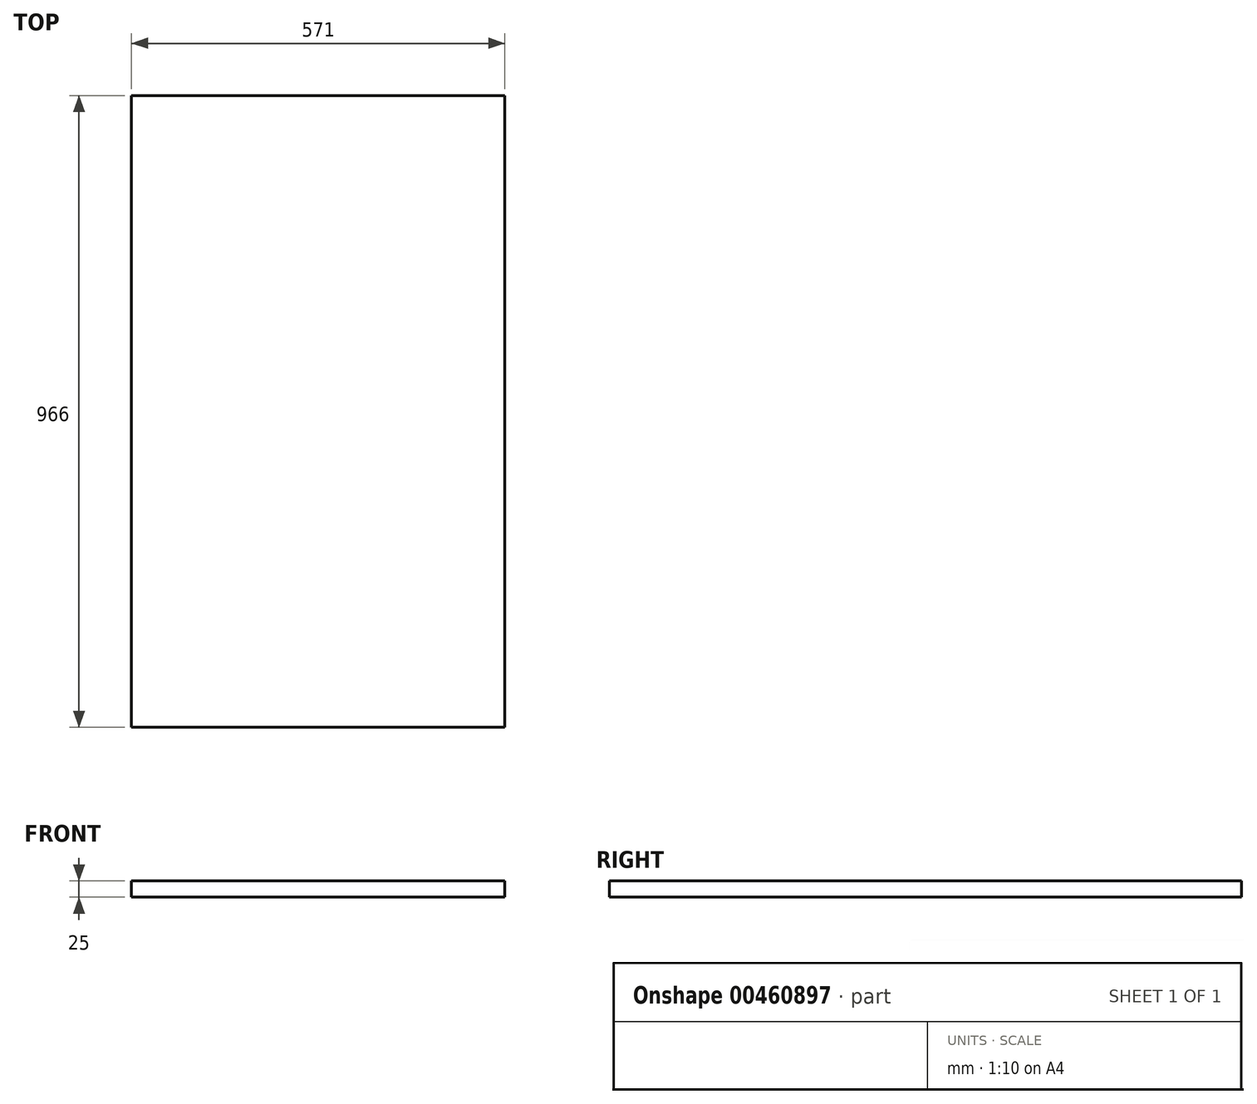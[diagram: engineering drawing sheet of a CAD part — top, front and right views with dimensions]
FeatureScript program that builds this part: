
annotation { "Feature Type Name" : "Feature", "Feature Type Description" : "" }
export const myFeature = defineFeature(function(context is Context, id is Id, definition is map)
    precondition{}
    {
        {
            var Q0;
            Q0=qCreatedBy(makeId("Top.planeOp"),FACE);
            var sketch = newSketch(context, id + "F0", { "sketchPlane" : qUnion([Q0])});
            skLineSegment(sketch, "E0.bottom", {"start": v(-473, 707.5) * mm, "end": v(104, 707.5) * mm});
            skLineSegment(sketch, "E0.top", {"start": v(-473, -264.5) * mm, "end": v(104, -264.5) * mm});
            skLineSegment(sketch, "E0.left", {"start": v(-473, 707.5) * mm, "end": v(-473, -264.5) * mm});
            skLineSegment(sketch, "E0.right", {"start": v(104, 707.5) * mm, "end": v(104, -264.5) * mm});
            skLineSegment(sketch, "E1.bottom", {"start": v(-470, 704.5) * mm, "end": v(101, 704.5) * mm});
            skLineSegment(sketch, "E1.top", {"start": v(-470, -261.5) * mm, "end": v(101, -261.5) * mm});
            skLineSegment(sketch, "E1.left", {"start": v(-470, 704.5) * mm, "end": v(-470, -261.5) * mm});
            skLineSegment(sketch, "E1.right", {"start": v(101, 704.5) * mm, "end": v(101, -261.5) * mm});
            skSolve(sketch);
        }
        {
            var Q0;
            Q0=makeQuery(id+"F0.imprint","IMPRINT",FACE,{"disambiguationData":[TD([[makeQuery(id+"F0.imprint","IMPRINT",EDGE,{"derivedFrom":sQuery(id+"F0.wireOp",EDGE,"E1.bottom")}),-1.0]])]});
            extrude(context, id + "F1", {"entities" : qUnion([Q0]), "depth" : 25 * mm});
        }
    });
